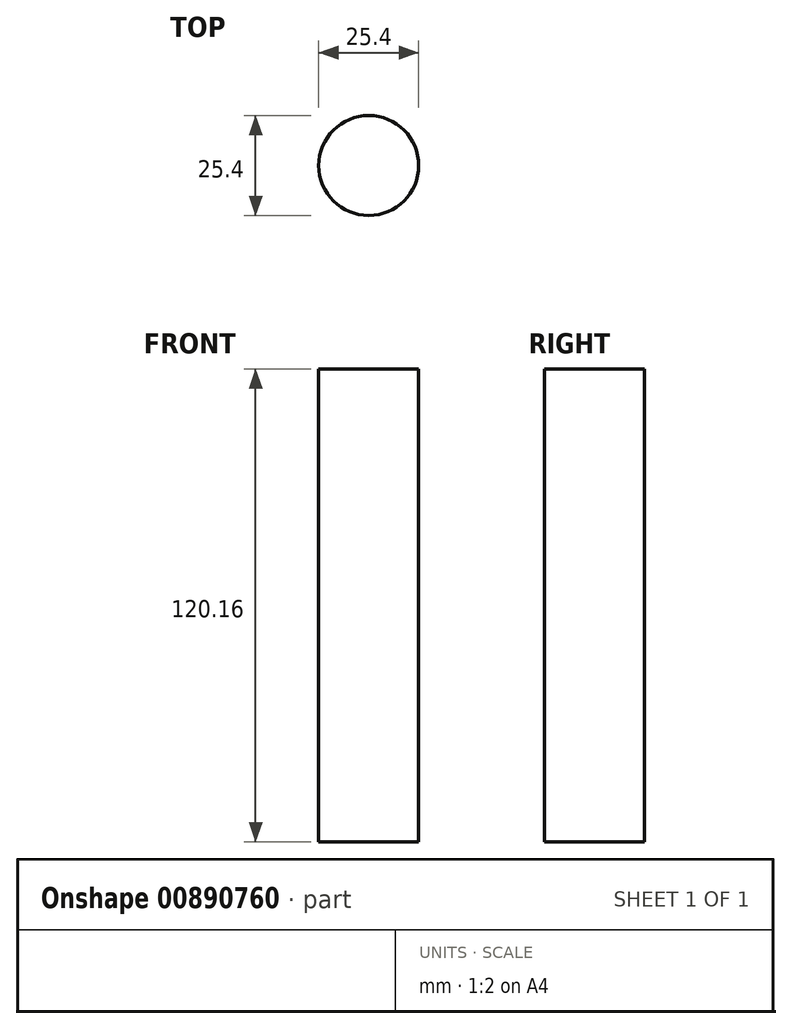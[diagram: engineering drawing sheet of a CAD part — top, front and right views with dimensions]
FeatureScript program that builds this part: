
annotation { "Feature Type Name" : "Feature", "Feature Type Description" : "" }
export const myFeature = defineFeature(function(context is Context, id is Id, definition is map)
    precondition{}
    {
        {
            var Q0;
            Q0=qCreatedBy(makeId("Front.planeOp"),FACE);
            var sketch = newSketch(context, id + "F0", { "sketchPlane" : qUnion([Q0])});
            skLineSegment(sketch, "E0.bottom", {"start": v(-6.35, -60.08) * mm, "end": v(6.35, -60.08) * mm});
            skLineSegment(sketch, "E0.top", {"start": v(-6.35, 60.08) * mm, "end": v(6.35, 60.08) * mm});
            skLineSegment(sketch, "E0.left", {"start": v(-6.35, -60.08) * mm, "end": v(-6.35, 60.08) * mm});
            skLineSegment(sketch, "E0.right", {"start": v(6.35, -60.08) * mm, "end": v(6.35, 60.08) * mm});
            skPoint(sketch, "E0.middle", {"position": v(0, 0) * mm});
            skSolve(sketch);
        }
        {
            var Q0;
            Q0=makeQuery(id+"F0.imprint","IMPRINT",FACE,{"disambiguationData":[TD([[makeQuery(id+"F0.imprint","IMPRINT",EDGE,{"derivedFrom":sQuery(id+"F0.wireOp",EDGE,"E0.bottom")}),1.0]])]});
            var Q1;
            Q1=sQuery(id+"F0.wireOp",EDGE,"E0.left");
            revolve(context, id + "F1", {"surfaceOperationType" : NewSurfaceOperationType.NEW, "entities" : qUnion([Q0]), "axis" : qUnion([Q1]), "revolveType" : RevolveType.FULL});
        }
        {
            var Q0;
            Q0=makeQuery(id+"F1.opRevolve","SWEPT_FACE",FACE,{"disambiguationData":[OSD([sQuery(id+"F0.wireOp",EDGE,"E0.top")])]});
            var sketch = newSketch(context, id + "F2", { "sketchPlane" : qUnion([Q0])});
            skCircle(sketch, "E1", {"center": v(-6.35, 0) * mm, "radius": 10.8 * mm});
            skSolve(sketch);
        }
        {
            var Q0;
            Q0=makeQuery(id+"F2.imprint","IMPRINT",FACE,{"disambiguationData":[TD([[makeQuery(id+"F2.imprint","IMPRINT",EDGE,{"derivedFrom":sQuery(id+"F2.wireOp",EDGE,"E1")}),1.0]])]});
            var Q1;
            Q1=sQuery(id+"F2.wireOp",EDGE,"E1");
            extrude(context, id + "F3", {"entities" : qUnion([Q0]), "bodyType" : ToolBodyType.SURFACE, "surfaceEntities" : qUnion([Q1]), "depth" : 254 * mm, "offsetDistance" : 25.4 * mm});
        }
    });
